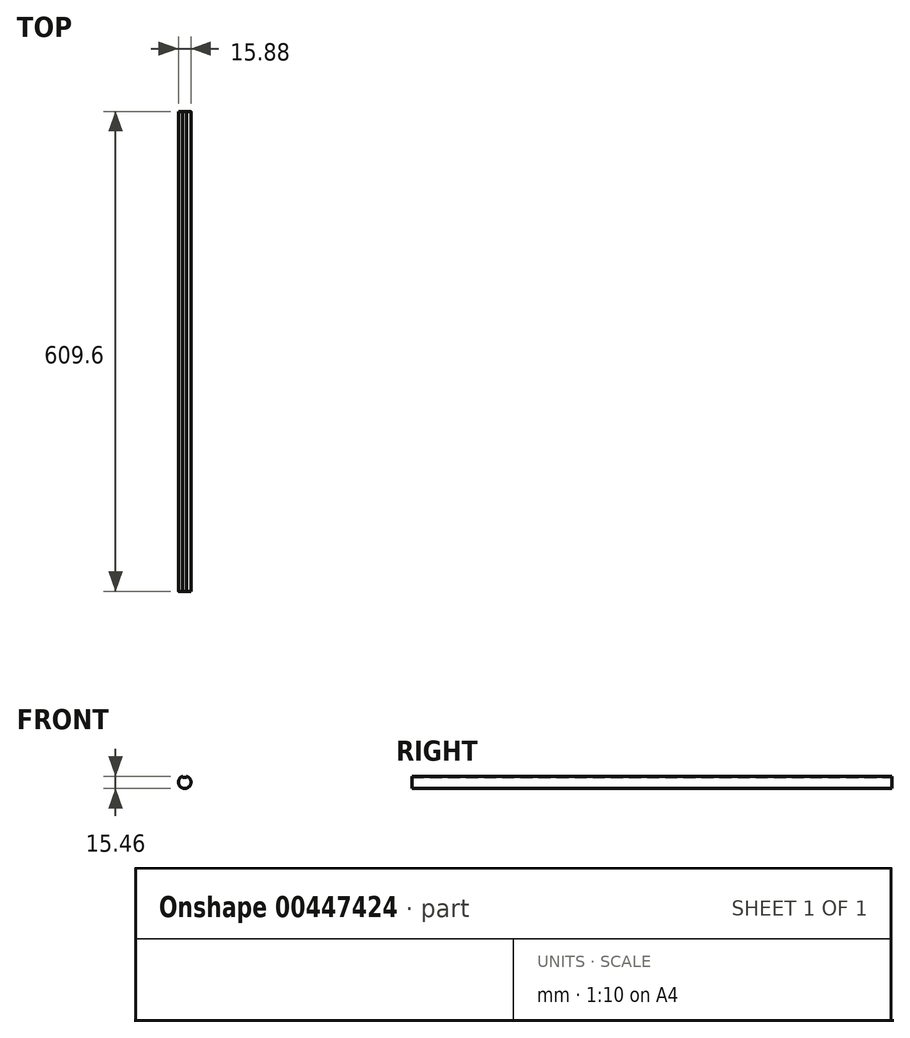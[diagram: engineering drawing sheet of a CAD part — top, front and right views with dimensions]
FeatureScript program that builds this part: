
annotation { "Feature Type Name" : "Feature", "Feature Type Description" : "" }
export const myFeature = defineFeature(function(context is Context, id is Id, definition is map)
    precondition{}
    {
        {
            var Q0;
            Q0=qCreatedBy(makeId("Front.planeOp"),FACE);
            var sketch = newSketch(context, id + "F0", { "sketchPlane" : qUnion([Q0])});
            skCircle(sketch, "E0", {"center": v(0, 0) * mm, "radius": 7.94 * mm});
            skSolve(sketch);
        }
        {
            var Q0;
            Q0=makeQuery(id+"F0.imprint","IMPRINT",FACE,{"disambiguationData":[TD([[makeQuery(id+"F0.imprint","IMPRINT",EDGE,{"derivedFrom":sQuery(id+"F0.wireOp",EDGE,"E0")}),1.0]])]});
            extrude(context, id + "F1", {"entities" : qUnion([Q0]), "depth" : 609.6 * mm});
        }
        {
            var Q0;
            Q0=qCreatedBy(makeId("Front.planeOp"),FACE);
            var sketch = newSketch(context, id + "F2", { "sketchPlane" : qUnion([Q0])});
            skLineSegment(sketch, "E1", {"start": v(0, 0) * mm, "end": v(0, 16) * mm});
            skLineSegment(sketch, "E2", {"start": v(0, 16) * mm, "end": v(2.54, 16) * mm});
            skLineSegment(sketch, "E3", {"start": v(2.54, 16) * mm, "end": v(2.54, 5.84) * mm});
            skLineSegment(sketch, "E4", {"start": v(2.54, 5.84) * mm, "end": v(-2.54, 5.84) * mm});
            skLineSegment(sketch, "E5", {"start": v(-2.54, 5.84) * mm, "end": v(-2.54, 16) * mm});
            skLineSegment(sketch, "E6", {"start": v(-2.54, 16) * mm, "end": v(0, 16) * mm});
            skSolve(sketch);
        }
        {
            var Q0;
            {var subQ0=sQuery(id+"F2.wireOp",EDGE,"E2");Q0=makeQuery(id+"F2.imprint","IMPRINT",FACE,{"disambiguationData":[TD([[makeQuery(id+"F2.imprint","IMPRINT",EDGE,{"derivedFrom":subQ0}),-1.0]])]});}
            var Q1;
            {var subQ4=sQuery(id+"F2.wireOp",EDGE,"E5");Q1=makeQuery(id+"F2.imprint","IMPRINT",FACE,{"disambiguationData":[TD([[makeQuery(id+"F2.imprint","IMPRINT",EDGE,{"derivedFrom":subQ4}),-1.0]])]});}
            extrude(context, id + "F3", {"entities" : qUnion([Q0, Q1]), "operationType" : NewBodyOperationType.REMOVE, "depth" : 711.2 * mm});
        }
    });
